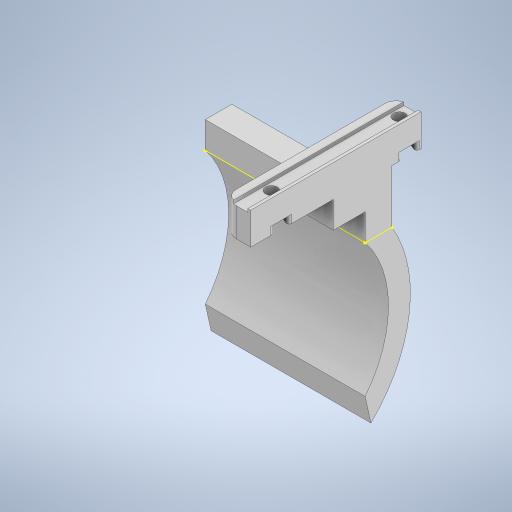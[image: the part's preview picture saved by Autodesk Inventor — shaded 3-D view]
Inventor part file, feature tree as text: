
AUTODESK INVENTOR PART (.ipt)
format: ipt  version: 2024 (Build 280153000, 153)  size: 340,480 bytes
history: native  units: in
note: dims shown in document units (in); Inventor stores cm internally (conversion verified against a paired STEP export)
features: sketch x8, extrude x5, projected_geometry x4, fillet x2, sweep x1
ambient origin geometry x8: Origin, YZ Plane, XZ Plane, XY Plane, X Axis, Y Axis, Z Axis, Center Point
bodies: Solid1 (feature_tree)
feature tree (20):
  extrude  "Extrusion1"  Depth=2.5197in
  extrude  "Extrusion2"  Depth=1.8898in
  extrude  "Extrusion3"  Depth=0.4724in TaperAngle=0.0deg
  fillet  "Fillet1"  Radius=0.0433in
  fillet  "Fillet2"  Radius=0.2126in
  extrude  "Extrusion17"  Depth=0.4724in TaperAngle=0.0deg
  extrude  "Extrusion18"  Depth=0.1181in TaperAngle=0.0deg
  sketch  "Sketch19"  dims[d17=0.1772in d18=0.0394in]
  sketch  "Sketch20"  dims[d19=0.1575in d76=0.4724in d90=0.102in d91=0.8661in d92=0.3937in d93=0.0in d94=2.3622in d95=0.3937in d96=0.3937in d97=0.0in d98=1.9685in d99=1.5748in d100=0.0in d101=0.0in d42=0.0197in d43=0.0344in d44=0.0197in d45=0.0344in d46=0.0in d47=0.0in d48=0.0in d49=0.0in d50=0.0in d51=0.0in d52=0.0in d53=0.0in d55=0.0197in d56=0.0344in d57=0.0197in d58=0.0344in d60=0.0197in d61=0.0344in d62=0.0197in d63=0.0344in d72=0.0197in d73=0.0344in d74=0.0197in d75=0.0344in]
  sketch  "3D Sketch1"
  sweep  "Sweep1"
  sketch  "Sketch1"  dims[d1=0.374in d2=2.5197in]
  sketch  "Sketch2"  dims[d3=0.1772in d4=1.8898in]
  sketch  "Sketch3"  dims[d6=0.1457in d7=0.4724in d8=0.0in d9=0.0433in d10=0.2126in]
  projected_geometry  "Projected Loop2"
  projected_geometry  "Projected Loop3"
  projected_geometry  "Projected Loop4"
  projected_geometry  "Projected Loop5"
  sketch  "Sketch17"  dims[d11=0.0472in d12=0.4724in d13=0.0in]
  sketch  "Sketch18"  dims[d14=0.2953in d15=0.1181in d16=0.0in]
